# Revit family: LR1680-T-2
name_source: partatom
category: Plumbing Fixtures
revit_build: Autodesk Revit 2018 (Build: 20170223_1515(x64)
units: mm (PartAtom-declared; Revit-internal decimal feet)

## family parameters
Cut with Voids When Loaded = No
Host = Face
OmniClass Number = 23.45.05.21.11.11
OmniClass Title = Water Operated Water Closets
Part Type = Normal
Room Calculation Point = No
Round Connector Dimension = Use Diameter
Shared = Yes

## types (1)
- LR1680-T-2
    1.28 GPF (HET) = No
    1.6 GPF (Not Available in California) = No
    2 On-Floor, Wall Outlet = Yes
    ADA - 18" Integral Seat Height = No
    Amperage = 0
    Assembly Code = D2010110
    CO1 - Cleanout w/ O-Ring Connecting to No-Hub 4" (Plain End Only) = No
    CO1-3 Cleanout w/ O-Ring Connecting to No-Hub 3” (Plain End Only) = No
    COH - Cleanout Hook Assembly = No
    CW Connection = Yes
    CWFU = 10
    Connection Size = 2 3/8"
    Default Elevation = 15"
    Description = Ligature Resistant Siphon Jet Toilet- On The Floor
    EG -  Enviro-Glaze Color Specify Toilet Interior & Exterior = No
    EGE -  Enviro-Glaze Color Specify Toilet Exterior Only = No
    EVSFV - Master-Trol Flush Valve (N/A for Top Supply) = No
    EVSPFV - Master-trol Electronic Flush Valve w/ Piezo Pushbutton (N/A for Top Supply) = No
    FT - Flood-Trol (N/A for Top Supply) = No
    FTA - Flood-Trol Auto-Reset (N/A for Top Supply) = No
    FTE - Flood-Trol, Electronic = No
    FV - Flush Valve, Mechanical (N/A for Top Supply, Accessory Options or ADA) = No
    FVBO - Flush Valve by Others = No
    FVH - Flush Valve, Hydraulic (N/A for Top Supply) = No
    FVT - Flush Valve Thru Wall Connection = No
    GW - Gasket Waste (Standard on-FM but Optinoal on-RM) = No
    HPS - High Polish Integral Seat = No
    HW Connection = Yes
    HWFU = 0
    Inlet Diameter Connection = 1 1/2"
    Installation Type = Wall Mounted
    LR1680 -  Ligature Resistant Siphon Jet Toilet = Yes
    Length = 29"
    MT - Metal Template (Only 1 Required Per Project) = No
    MTPFV - Master-Trol® PLUS Electronic Flush Valve (N/A for Top Supply) = No
    MTPPFV - Master-Trol® PLUS Electronic Flush Valve w/ Piezo Button (N/A for Top Supply) = No
    MVCFV - Time-Trol Electronic FV (N/A for Top Supply) = No
    Manufacturer = Acorn
    Material = Metal Acorn 304 Stainless Steel
    Model = LR1680-T-2
    PC Pinned Cleanout Plug (For -CO1 Options above) = No
    Product Documentation Link = https://www.acorneng.com
    Product Page URL = https://www.acorneng.com
    SW - Wall Sleeve = No
    T - Top (Exposed) = Yes
    TF Transformer, 120VAC to 24VAC (-MVCFV option) = No
    TG - Twelve Gage Housing = No
    TSC - Toilet Shipping Cover = No
    TWE - Toilet Waste Extension (3" Standard) (Specify Length Beyond Fixture) = No
    Tempered Water Connection = No
    URL = www.acorneng.com
    VAC - AcornVac System = No
    Vent Connection = No
    Voltage = 0
    W - Wall (Concealed) = No
    WFU = 10
    WO3B - 3" Bell Waste Outlet w/ Std. 2-3/8" Trap = No
    Warranty Documentation Link = www.acorneng.com/terms-and-conditions
    Waste Connection = Yes
    Width = 14 1/4"

## geometry (parser evidence)
native form markers: Sweep x3
no freeform markers — native parametric forms only
